# Revit family: Atlas_Sound_M2000-SM_Non-Hosted
name_source: partatom
category: Communication Devices
revit_build: Autodesk Revit 2016 (Build: 20161004_0715(x64)
units: mm (PartAtom-declared; Revit-internal decimal feet)

## family parameters
Always vertical = Yes
Cut with Voids When Loaded = No
Maintain Annotation Orientation = No
Part Type = Normal
Room Calculation Point = No
Round Connector Dimension = Use Diameter
Shared = No
Work Plane-Based = No

## types (1)
- Atlas_Sound_M2000-SM_Non-Hosted
    DIM = 3.5 "
    Description = Surface mounted sound masking transducer
    Expected Lifespan (Years) = 0
    Installation-Fabrication = https://www.atlasied.com
    Maintenance Schedule (Months) = 0
    Manufacturer = Atlas Sound
    Manufacturer Fax = 602-438-8692
    Manufacturer Website = https://www.atlasied.com
    Product Data = https://www.atlasied.com
    URL = https://www.atlasied.com
    Warranty Duration (Years) = 0

## geometry (parser evidence)
native form markers: Sweep x2
no freeform markers — native parametric forms only
